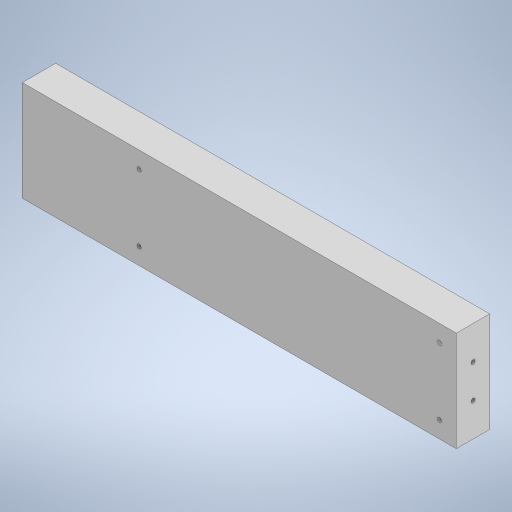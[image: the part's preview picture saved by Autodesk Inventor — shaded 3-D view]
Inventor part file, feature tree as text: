
AUTODESK INVENTOR PART (.ipt)
format: ipt  version: 2023 (Build 270158000, 158)  size: 374,784 bytes
history: native  units: in
note: dims shown in document units (in); Inventor stores cm internally (conversion verified against a paired STEP export)
features: extrude x5, sketch x5
ambient origin geometry x8: Origin, YZ Plane, XZ Plane, XY Plane, X Axis, Y Axis, Z Axis, Center Point
bodies: Solid1 (feature_tree)
feature tree (10):
  extrude  "Extrusion1"  Depth=54.0in
  extrude  "Extrusion2"  Depth=1.0in
  extrude  "Extrusion3"  Depth=16.0in
  extrude  "Extrusion4"  Depth=16.0in
  extrude  "Extrusion5"  Depth=3.0in
  sketch  "Sketch1"  dims[d0=54.0in d1=54.0in]
  sketch  "Sketch2"  dims[d2=1.0in d3=1.0in]
  sketch  "Sketch3"  dims[d4=8.0in d5=16.0in]
  sketch  "Sketch4"  dims[d6=8.0in d7=16.0in]
  sketch  "Sketch5"  dims[d8=16.0in d9=8.0in d10=16.0in d11=8.0in d12=4.0in d13=4.0in d14=4.0in d15=4.0in d16=17.0in d17=17.0in d18=17.0in d19=17.0in d20=20.0in d21=1.0in d22=1.0in d23=1.0in d24=1.0in d25=45.0deg d26=2.5in d27=45.0deg d28=45.0deg d29=45.0deg d30=1.0in d31=1.0in d32=1.0in d33=1.0in d34=0.25in d35=0.25in d36=0.25in d37=0.25in d38=0.25in d39=0.25in d40=0.25in d41=0.25in d42=3.0in d43=0.0in d44=0.125in d45=0.125in d46=0.5in d47=0.5in d48=0.5in d49=0.5in d50=1.0in d51=0.0in d52=0.125in d53=0.125in d54=0.5in d55=0.5in d56=0.5in d57=0.5in d58=2.0in d59=0.0in d60=0.125in d61=0.125in d62=0.5in d63=0.5in d64=1.0in d65=1.0in d66=1.0in d67=0.0in d68=0.125in d69=0.125in d70=0.5in d71=0.5in d72=0.5in d73=0.5in d74=3.0in d75=0.0in]
